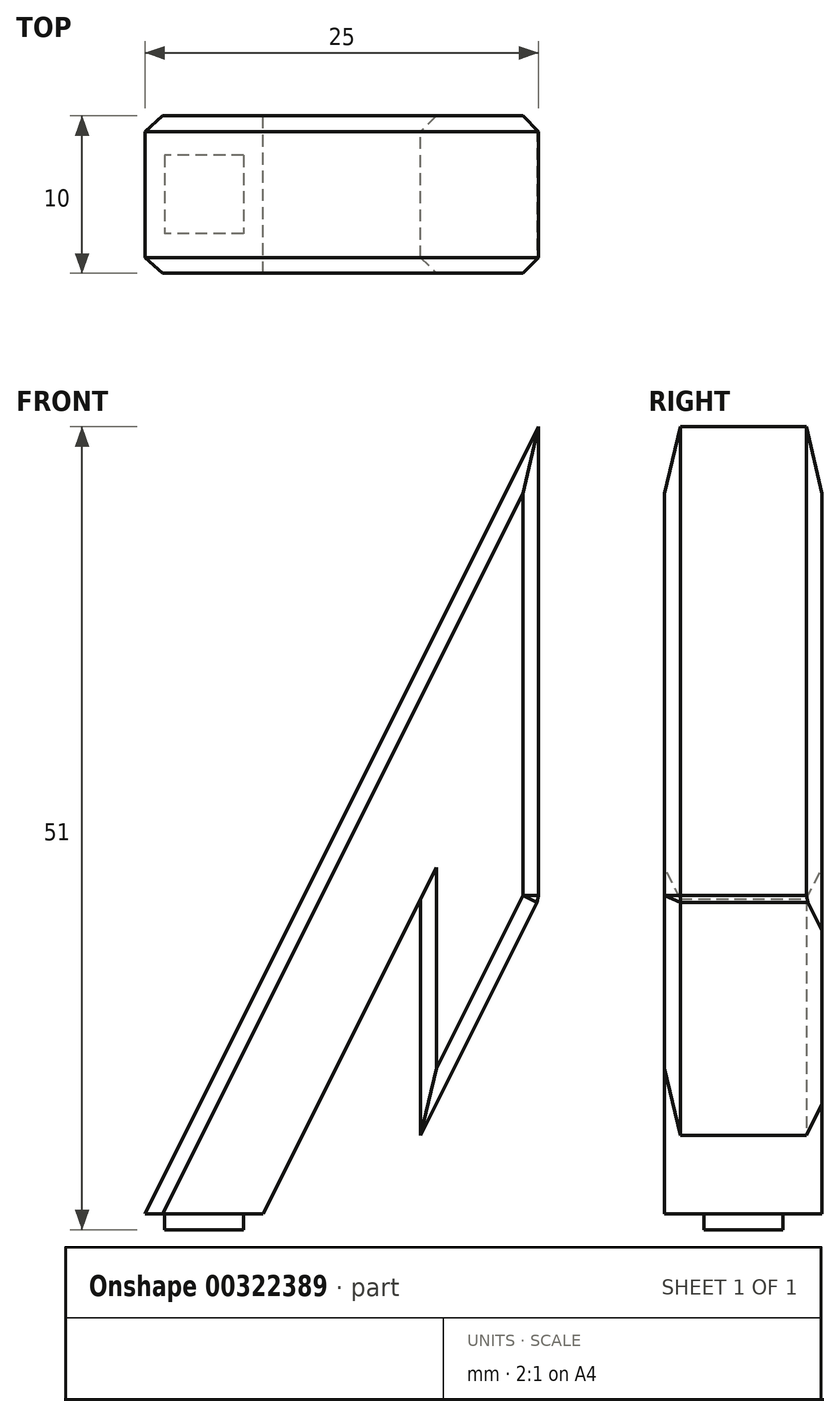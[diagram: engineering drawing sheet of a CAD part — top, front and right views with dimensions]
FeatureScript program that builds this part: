
annotation { "Feature Type Name" : "Feature", "Feature Type Description" : "" }
export const myFeature = defineFeature(function(context is Context, id is Id, definition is map)
    precondition{}
    {
        {
            var Q0;
            Q0=qCreatedBy(makeId("Front.planeOp"),FACE);
            var sketch = newSketch(context, id + "F0", { "sketchPlane" : qUnion([Q0])});
            skLineSegment(sketch, "E0", {"start": v(0, 50) * mm, "end": v(-25, 0) * mm});
            skLineSegment(sketch, "E1", {"start": v(-25, 0) * mm, "end": v(0, 0) * mm});
            skLineSegment(sketch, "E2", {"start": v(0, 0) * mm, "end": v(0, 50) * mm});
            skLineSegment(sketch, "E3", {"start": v(-7.5, 20) * mm, "end": v(-17.5, 0) * mm});
            skLineSegment(sketch, "E4", {"start": v(-17.5, 0) * mm, "end": v(-7.5, 20) * mm});
            skLineSegment(sketch, "E5", {"start": v(-7.5, 20) * mm, "end": v(-7.5, 0) * mm});
            skLineSegment(sketch, "E6", {"start": v(-7.5, 0) * mm, "end": v(-17.5, 0) * mm});
            skLineSegment(sketch, "E7", {"start": v(-7.5, 5) * mm, "end": v(0, 20) * mm});
            skSolve(sketch);
        }
        {
            var Q0;
            {var subQ1=sQuery(id+"F0.wireOp",EDGE,"E0");Q0=makeQuery(id+"F0.imprint","IMPRINT",FACE,{"disambiguationData":[TD([[makeQuery(id+"F0.imprint","IMPRINT",EDGE,{"derivedFrom":subQ1}),1.0]])]});}
            extrude(context, id + "F1", {"entities" : qUnion([Q0]), "depth" : 10 * mm});
        }
        {
            var Q0;
            Q0=makeQuery(id+"F1.opExtrude","CAP_EDGE",EDGE,{"disambiguationData":[OSD([sQuery(id+"F0.wireOp",EDGE,"E4")])],"isStart":false});
            var Q1;
            Q1=makeQuery(id+"F1.opExtrude","CAP_EDGE",EDGE,{"disambiguationData":[OSD([sQuery(id+"F0.wireOp",EDGE,"E0")])],"isStart":false});
            var Q2;
            Q2=makeQuery(id+"F1.opExtrude","CAP_EDGE",EDGE,{"disambiguationData":[OSD([sQuery(id+"F0.wireOp",EDGE,"E4")])],"isStart":true});
            var Q3;
            Q3=makeQuery(id+"F1.opExtrude","CAP_EDGE",EDGE,{"disambiguationData":[OSD([sQuery(id+"F0.wireOp",EDGE,"E0")])],"isStart":true});
            var Q4;
            Q4=makeQuery(id+"F1.opExtrude","CAP_EDGE",EDGE,{"disambiguationData":[OSD([sQuery(id+"F0.wireOp",EDGE,"E5")])],"isStart":true});
            var Q5;
            Q5=makeQuery(id+"F1.opExtrude","CAP_EDGE",EDGE,{"disambiguationData":[OSD([sQuery(id+"F0.wireOp",EDGE,"E5")])],"isStart":false});
            var Q6;
            Q6=makeQuery(id+"F1.opExtrude","CAP_EDGE",EDGE,{"disambiguationData":[OSD([sQuery(id+"F0.wireOp",EDGE,"E2")])],"isStart":false});
            var Q7;
            Q7=makeQuery(id+"F1.opExtrude","CAP_EDGE",EDGE,{"disambiguationData":[OSD([sQuery(id+"F0.wireOp",EDGE,"E7")])],"isStart":false});
            var Q8;
            Q8=makeQuery(id+"F1.opExtrude","SWEPT_EDGE",EDGE,{"disambiguationData":[OSD([sQuery(id+"F0.wireOp",EDGE,"E2"),sQuery(id+"F0.wireOp",EDGE,"E7")])]});
            var Q9;
            Q9=makeQuery(id+"F1.opExtrude","CAP_EDGE",EDGE,{"disambiguationData":[OSD([sQuery(id+"F0.wireOp",EDGE,"E2")])],"isStart":true});
            chamfer(context, id + "F2", {"entities" : qUnion([Q0, Q1, Q2, Q3, Q4, Q5, Q6, Q7, Q8, Q9]), "width" : 1 * mm, "tangentPropagation" : true});
        }
        {
            var Q0;
            Q0=makeQuery(id+"F1.opExtrude","SWEPT_FACE",FACE,{"disambiguationData":[OSD([sQuery(id+"F0.wireOp",EDGE,"E1")])]});
            var sketch = newSketch(context, id + "F3", { "sketchPlane" : qUnion([Q0])});
            skLineSegment(sketch, "E8.bottom", {"start": v(-18.75, 2.5) * mm, "end": v(-23.75, 2.5) * mm});
            skLineSegment(sketch, "E8.top", {"start": v(-18.75, 7.5) * mm, "end": v(-23.75, 7.5) * mm});
            skLineSegment(sketch, "E8.left", {"start": v(-18.75, 2.5) * mm, "end": v(-18.75, 7.5) * mm});
            skLineSegment(sketch, "E8.right", {"start": v(-23.75, 2.5) * mm, "end": v(-23.75, 7.5) * mm});
            skPoint(sketch, "E8.middle", {"position": v(-21.25, 5) * mm});
            skLineSegment(sketch, "E9", {"start": v(-21.25, 7.5) * mm, "end": v(-21.25, 10) * mm});
            skLineSegment(sketch, "E10", {"start": v(-18.75, 5) * mm, "end": v(-17.5, 5) * mm});
            skLineSegment(sketch, "E11", {"start": v(-21.25, 2.5) * mm, "end": v(-21.25, 0) * mm});
            skLineSegment(sketch, "E12", {"start": v(-23.75, 5) * mm, "end": v(-25, 5) * mm});
            skSolve(sketch);
        }
        {
            var Q0;
            {var subQ4=sQuery(id+"F3.wireOp",EDGE,"E8.left");var subQ6=sQuery(id+"F3.wireOp",EDGE,"E8.bottom");var subQ9=makeQuery(id+"F3.imprint","INTERSECT",VERTEX,{"derivedFrom":[subQ6,subQ4]});Q0=makeQuery(id+"F3.imprint","IMPRINT",FACE,{"disambiguationData":[TD([[makeQuery(id+"F3.imprint","IMPRINT",EDGE,{"disambiguationData":[TD([[subQ9,-1.0]])],"derivedFrom":subQ6}),-1.0]])]});}
            extrude(context, id + "F4", {"entities" : qUnion([Q0]), "operationType" : NewBodyOperationType.ADD, "depth" : 1 * mm});
        }
    });
